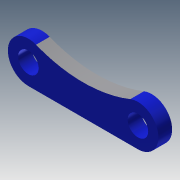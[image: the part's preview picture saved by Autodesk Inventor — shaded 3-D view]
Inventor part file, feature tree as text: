
AUTODESK INVENTOR PART (.ipt)
format: ipt  version: 2013 (Build 170138000, 138)  size: 136,704 bytes
history: native  units: mm
features: extrude x7, sketch x7
ambient origin geometry x8: Origin, YZ Plane, XZ Plane, XY Plane, X Axis, Y Axis, Z Axis, Center Point
bodies: Solid1 (feature_tree)
feature tree (14):
  extrude  "Extrusion1"  Depth=6.0mm
  extrude  "Extrusion2"  Depth=6.0mm
  extrude  "Extrusion3"  Depth=3.0mm
  extrude  "Extrusion4"  Depth=2.0mm TaperAngle=0.0deg
  extrude  "Extrusion5"  Depth=2.0mm TaperAngle=0.0deg
  extrude  "Extrusion6"  Depth=2.0mm TaperAngle=0.0deg
  extrude  "Extrusion7"  Depth=6.0mm
  sketch  "Sketch1"  dims[d0=16.0mm d1=6.0mm]
  sketch  "Sketch2"  dims[d2=6.0mm d3=6.0mm]
  sketch  "Sketch3"  dims[d4=2.0mm d5=0.0mm d6=3.0mm]
  sketch  "Sketch4"  dims[d7=3.0mm d8=2.0mm d9=0.0mm]
  sketch  "Sketch5"  dims[d11=20.0mm d12=2.0mm d13=0.0mm]
  sketch  "Sketch6"  dims[d14=2.0mm d15=0.0mm d16=2.0mm d17=0.0mm]
  sketch  "Sketch7"  dims[d18=2.0mm d19=0.0mm d20=6.0mm d21=3.0mm d22=3.0mm d23=2.0mm d24=0.0mm]
